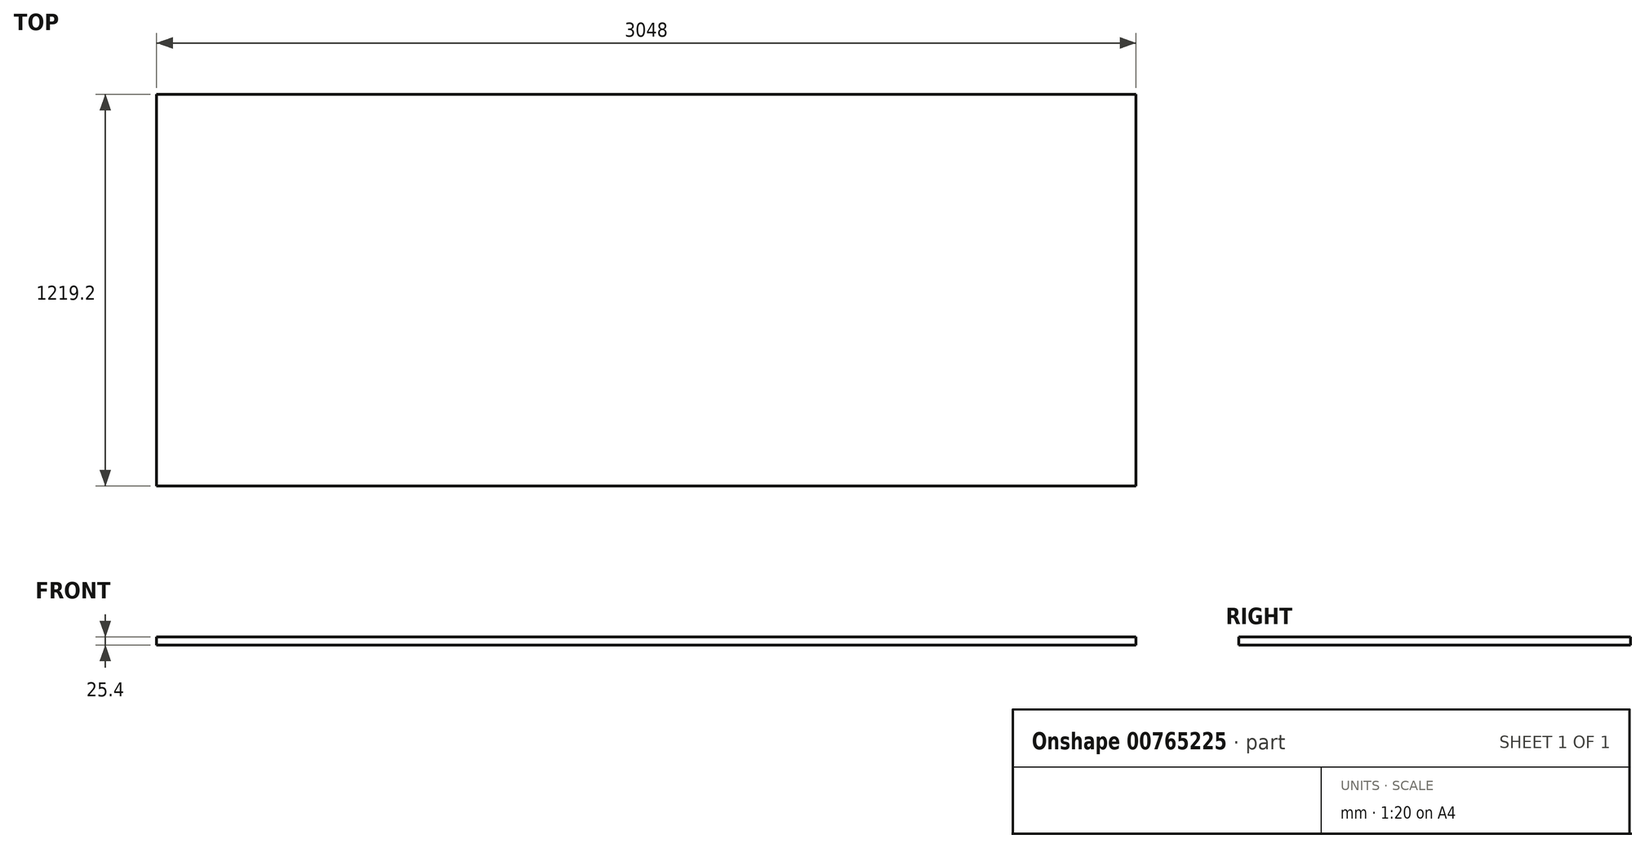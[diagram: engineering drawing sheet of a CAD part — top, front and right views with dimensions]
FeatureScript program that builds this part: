
annotation { "Feature Type Name" : "Feature", "Feature Type Description" : "" }
export const myFeature = defineFeature(function(context is Context, id is Id, definition is map)
    precondition{}
    {
        {
            var Q0;
            Q0=qCreatedBy(makeId("Top.planeOp"),FACE);
            var sketch = newSketch(context, id + "F0", { "sketchPlane" : qUnion([Q0])});
            skLineSegment(sketch, "E0.bottom", {"start": v(-1524, 609.6) * mm, "end": v(1524, 609.6) * mm});
            skLineSegment(sketch, "E0.top", {"start": v(-1524, -609.6) * mm, "end": v(1524, -609.6) * mm});
            skLineSegment(sketch, "E0.left", {"start": v(-1524, 609.6) * mm, "end": v(-1524, -609.6) * mm});
            skLineSegment(sketch, "E0.right", {"start": v(1524, 609.6) * mm, "end": v(1524, -609.6) * mm});
            skSolve(sketch);
        }
        {
            var Q0;
            Q0=makeQuery(id+"F0.imprint","IMPRINT",FACE,{"disambiguationData":[TD([[makeQuery(id+"F0.imprint","IMPRINT",EDGE,{"derivedFrom":sQuery(id+"F0.wireOp",EDGE,"E0.bottom")}),-1.0]])]});
            extrude(context, id + "F1", {"entities" : qUnion([Q0]), "endBound" : BoundingType.SYMMETRIC, "depth" : 25.4 * mm, "offsetDistance" : 25.4 * mm});
        }
    });
